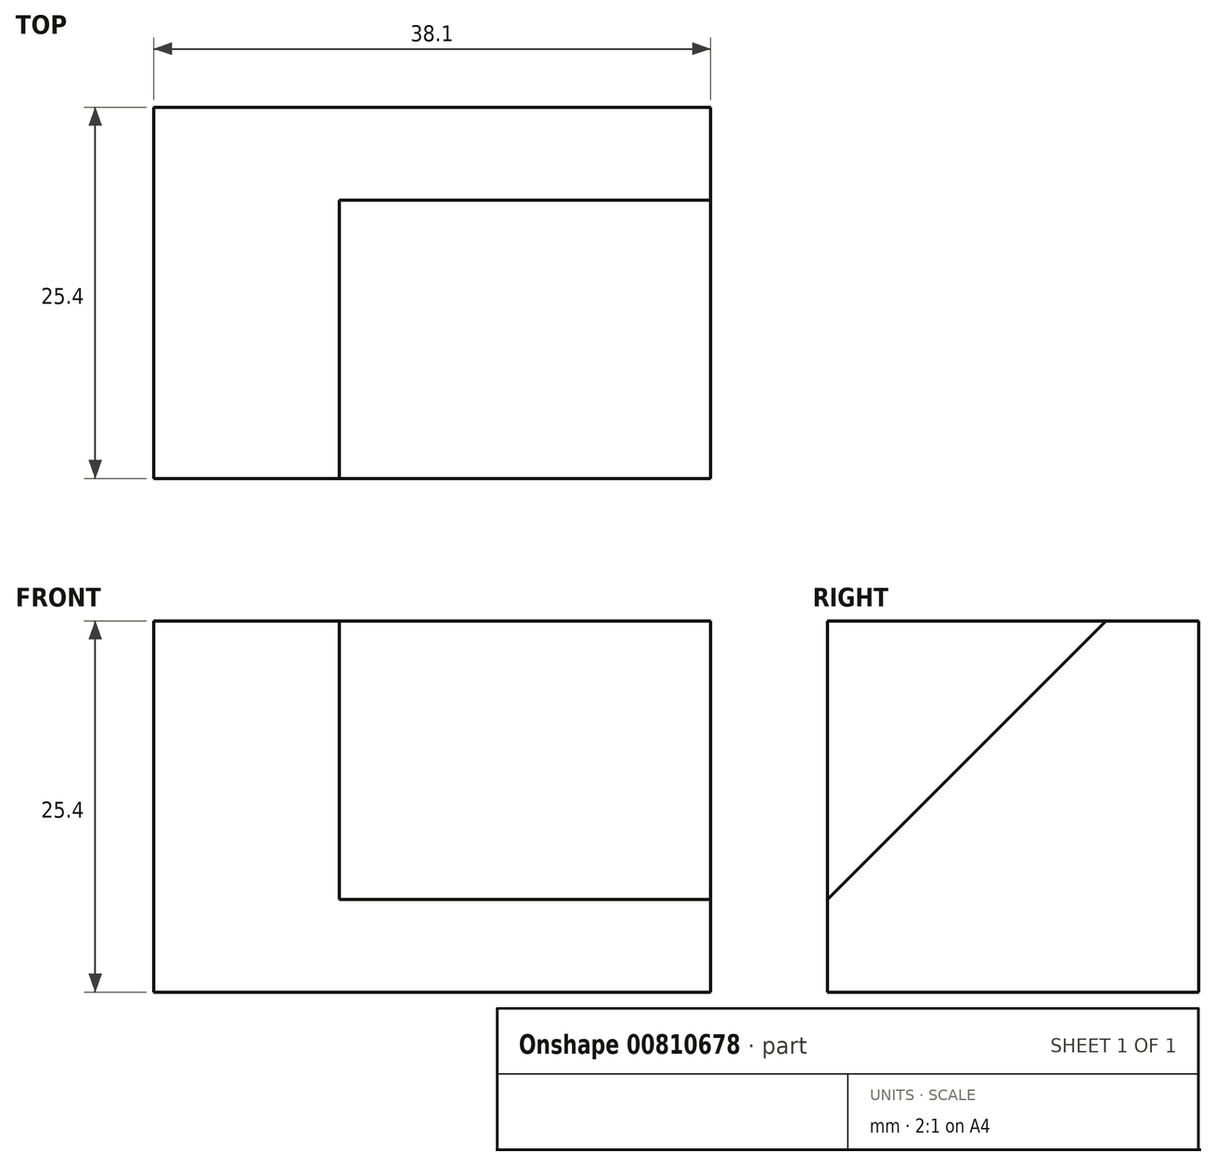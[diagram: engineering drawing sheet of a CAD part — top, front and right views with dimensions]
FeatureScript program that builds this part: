
annotation { "Feature Type Name" : "Feature", "Feature Type Description" : "" }
export const myFeature = defineFeature(function(context is Context, id is Id, definition is map)
    precondition{}
    {
        {
            var Q0;
            Q0=qCreatedBy(makeId("Top.planeOp"),FACE);
            var sketch = newSketch(context, id + "F0", { "sketchPlane" : qUnion([Q0])});
            skLineSegment(sketch, "E0.bottom", {"start": v(0, 0) * mm, "end": v(0, 0) * mm});
            skLineSegment(sketch, "E1.bottom", {"start": v(0, 0) * mm, "end": v(38.1, 0) * mm});
            skLineSegment(sketch, "E1.top", {"start": v(0, 25.4) * mm, "end": v(38.1, 25.4) * mm});
            skLineSegment(sketch, "E1.left", {"start": v(0, 0) * mm, "end": v(0, 25.4) * mm});
            skLineSegment(sketch, "E1.right", {"start": v(38.1, 0) * mm, "end": v(38.1, 25.4) * mm});
            skSolve(sketch);
        }
        {
            var Q0;
            Q0 = qSketchRegion(id + "F0", true);
            extrude(context, id + "F1", {"entities" : qUnion([Q0]), "depth" : 25.4 * mm, "offsetDistance" : 25.4 * mm});
        }
        {
            var Q0;
            Q0=makeQuery(id+"F1.opExtrude","SWEPT_FACE",FACE,{"disambiguationData":[OSD([sQuery(id+"F0.wireOp",EDGE,"E1.right")])]});
            var sketch = newSketch(context, id + "F2", { "sketchPlane" : qUnion([Q0])});
            skLineSegment(sketch, "E2", {"start": v(25.4, 25.4) * mm, "end": v(19.05, 25.4) * mm});
            skLineSegment(sketch, "E3", {"start": v(0, 0) * mm, "end": v(0, 6.35) * mm});
            skLineSegment(sketch, "E4", {"start": v(0, 6.35) * mm, "end": v(19.05, 25.4) * mm});
            skSolve(sketch);
        }
        {
            var Q0;
            {var subQ0=sQuery(id+"F2.wireOp",EDGE,"E4");Q0=makeQuery(id+"F2.imprint","IMPRINT",FACE,{"disambiguationData":[TD([[makeQuery(id+"F2.imprint","IMPRINT",EDGE,{"derivedFrom":subQ0}),1.0]])]});}
            extrude(context, id + "F3", {"entities" : qUnion([Q0]), "operationType" : NewBodyOperationType.REMOVE, "oppositeDirection" : true, "depth" : 25.4 * mm, "offsetDistance" : 25.4 * mm});
        }
    });
